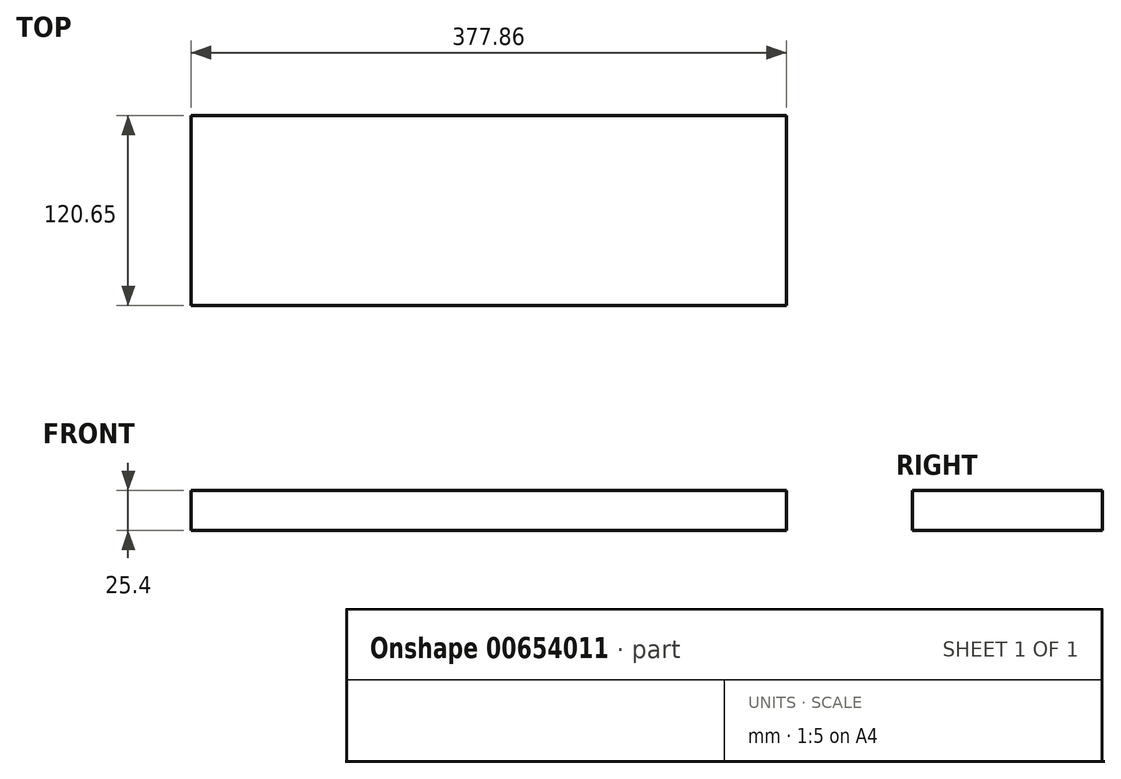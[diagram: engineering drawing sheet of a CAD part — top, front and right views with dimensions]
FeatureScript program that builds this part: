
annotation { "Feature Type Name" : "Feature", "Feature Type Description" : "" }
export const myFeature = defineFeature(function(context is Context, id is Id, definition is map)
    precondition{}
    {
        {
            var Q0;
            Q0=qCreatedBy(makeId("Top.planeOp"),FACE);
            var sketch = newSketch(context, id + "F0", { "sketchPlane" : qUnion([Q0])});
            skLineSegment(sketch, "E0.bottom", {"start": v(-188.4, -43.47) * mm, "end": v(189.45, -43.47) * mm});
            skLineSegment(sketch, "E0.top", {"start": v(-188.4, 77.18) * mm, "end": v(189.45, 77.18) * mm});
            skLineSegment(sketch, "E0.left", {"start": v(-188.4, -43.47) * mm, "end": v(-188.4, 77.18) * mm});
            skLineSegment(sketch, "E0.right", {"start": v(189.45, -43.47) * mm, "end": v(189.45, 77.18) * mm});
            skSolve(sketch);
        }
        {
            var Q0;
            Q0=makeQuery(id+"F0.imprint","IMPRINT",FACE,{"disambiguationData":[TD([[makeQuery(id+"F0.imprint","IMPRINT",EDGE,{"derivedFrom":sQuery(id+"F0.wireOp",EDGE,"E0.bottom")}),1.0]])]});
            extrude(context, id + "F1", {"entities" : qUnion([Q0]), "depth" : 25.4 * mm, "offsetDistance" : 25.4 * mm});
        }
    });
